# Revit family: IS_Attitude_A4601_BIM_FR
name_source: partatom
category: Plumbing Fixtures
revit_build: Autodesk Revit MEP 2016 (Build: 20161004_0715(x64)
units: mm (PartAtom-declared; Revit-internal decimal feet)

## family parameters
Cut with Voids When Loaded = No
Host = Face
OmniClass Number = 23.45.55.17
OmniClass Title = Mixing Faucets
Part Type = Normal
Room Calculation Point = No
Round Connector Dimension = Use Diameter
Shared = Yes

## types (1)
- A4601AA - ATTITUDE BSN MXR R-MTD VESSEL WTRFALL
    Accessoires = www.idealspec.fr
    Assembly Code = C1030200
    Bim-NomDuProjet = ISI_IdealStandard_Attitude_A4601
    CWFU = 0
    Caractéristiques = Mitigeur Lavabo Réhaussé Monotrou
    Conformité = NF
    ConseilsDInstallation = 0
    Cost = 0 $
    CoûtDeRemplacement = 0
    DateDeCréation = 43351
    Default Elevation = 800 mm  [stored 2.62467 ft]
    Description = Mitigeur Lavabo Réhaussé Monotrou
    Dimensions = 311 x 52 x 160 mm
    Espace = Interne
    Forme = Complexe
    HWFU = 0
    Hauteur = 311 mm  [stored 1.02034 ft]
    InformationsProduit = www.idealspec.fr
    Largeur = 52 mm
    Longueur = 160 mm  [stored 0.524934 ft]
    Marque = Ideal Standard
    Model = A4601GN
    NBSDescription = Water supply fittings for wash basins and troughs
    NBSReference = 45-35-70/371
    PoidsNet = 0
    Profondeur = 0 mm  [stored 0 ft]
    Raccordement = Plomberie
    Révision = 1
    URL = www.idealspec.fr
    Uniclass2015Code = Pr_40_20_87_98
    Uniclass2015Title = Washbasin taps
    UnitéDeMesure = Millimètres
    UnitéDeTemps = An
    UnitéMonétaire = €
    UrlDuFabricant = www.idealspec.fr
    WFU = 0

note: [stored X ft] marks values corroborated as IEEE doubles in the binary element streams (Revit-internal decimal feet)

## geometry (parser evidence)
native form markers: Blend x4, Sweep x1
no freeform markers — native parametric forms only
